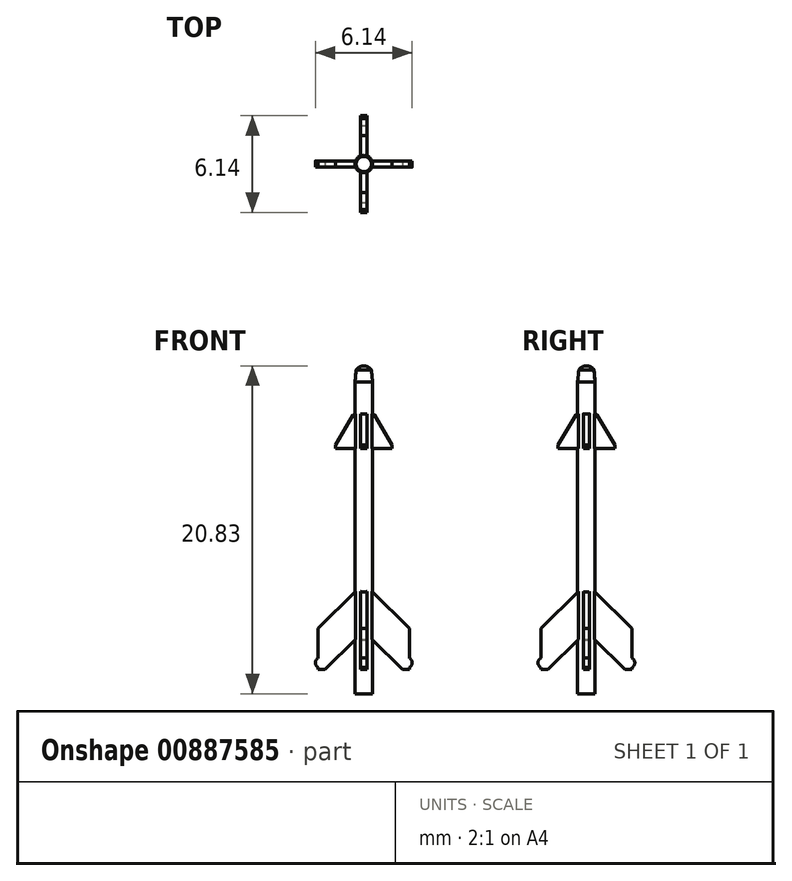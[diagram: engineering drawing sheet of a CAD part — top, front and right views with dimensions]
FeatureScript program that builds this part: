
annotation { "Feature Type Name" : "Feature", "Feature Type Description" : "" }
export const myFeature = defineFeature(function(context is Context, id is Id, definition is map)
    precondition{}
    {
        {
            var Q0;
            Q0=qCreatedBy(makeId("Front.planeOp"),FACE);
            var sketch = newSketch(context, id + "F0", { "sketchPlane" : qUnion([Q0])});
            skLineSegment(sketch, "E0", {"start": v(0, 0) * mm, "end": v(0, 20.83) * mm});
            skLineSegment(sketch, "E1", {"start": v(0.56, 19.8) * mm, "end": v(0.56, 0) * mm});
            skLineSegment(sketch, "E2", {"start": v(0.56, 0) * mm, "end": v(0, 0) * mm});
            skLineSegment(sketch, "E3", {"start": v(0, 20.83) * mm, "end": v(1.85, 20.83) * mm, "construction": true});
            skLineSegment(sketch, "E4", {"start": v(0.56, 19.8) * mm, "end": v(0.49, 20.56) * mm});
            skArc(sketch, "E5", {"start": v(0.49, 20.56) * mm, "mid": v(0.28, 20.76) * mm, "end": v(0, 20.83) * mm});
            skSolve(sketch);
        }
        {
            var Q0;
            Q0=qSketchRegion(id+"F0",true);
            var Q1;
            Q1=sQuery(id+"F0.wireOp",EDGE,"E0");
            revolve(context, id + "F1", {"surfaceOperationType" : NewSurfaceOperationType.NEW, "entities" : qUnion([Q0]), "axis" : qUnion([Q1]), "revolveType" : RevolveType.FULL});
        }
        {
            var Q0;
            Q0=qCreatedBy(makeId("Front.planeOp"),FACE);
            var sketch = newSketch(context, id + "F2", { "sketchPlane" : qUnion([Q0])});
            skLineSegment(sketch, "E6", {"start": v(0.38, 6.63) * mm, "end": v(-0.38, 6.63) * mm});
            skLineSegment(sketch, "E7", {"start": v(-2.9, 4.15) * mm, "end": v(-0.38, 6.63) * mm});
            skLineSegment(sketch, "E8", {"start": v(-2.9, 4.15) * mm, "end": v(-2.9, 2.27) * mm});
            skLineSegment(sketch, "E9", {"start": v(2.9, 2.27) * mm, "end": v(2.9, 4.15) * mm});
            skLineSegment(sketch, "E10", {"start": v(0.38, 6.63) * mm, "end": v(2.9, 4.15) * mm});
            skLineSegment(sketch, "E11", {"start": v(0, 0) * mm, "end": v(0, 6.63) * mm, "construction": true});
            skLineSegment(sketch, "E12", {"start": v(-0.56, -0.14) * mm, "end": v(-0.56, 4.02) * mm, "construction": true});
            skLineSegment(sketch, "E13.0", {"start": v(0.56, 19.8) * mm, "end": v(-0.56, 19.8) * mm});
            skPoint(sketch, "E14", {"position": v(-0.56, 6.46) * mm});
            skLineSegment(sketch, "E15", {"start": v(-2.9, 1.53) * mm, "end": v(-2.9, 1.67) * mm});
            skArc(sketch, "E16", {"start": v(-2.9, 2.27) * mm, "mid": v(-3.07, 1.97) * mm, "end": v(-2.9, 1.67) * mm});
            skArc(sketch, "E17", {"start": v(2.9, 1.67) * mm, "mid": v(3.07, 1.97) * mm, "end": v(2.9, 2.27) * mm});
            skLineSegment(sketch, "E18", {"start": v(-1.8, 15.6) * mm, "end": v(1.8, 15.6) * mm});
            skLineSegment(sketch, "E19", {"start": v(0, 15.6) * mm, "end": v(0, 0) * mm, "construction": true});
            skLineSegment(sketch, "E20", {"start": v(-0.56, 19.8) * mm, "end": v(-0.56, 14.02) * mm, "construction": true});
            skLineSegment(sketch, "E21", {"start": v(-1.8, 15.6) * mm, "end": v(-1.8, 15.8) * mm});
            skLineSegment(sketch, "E22", {"start": v(-1.8, 15.8) * mm, "end": v(-0.68, 17.7) * mm});
            skLineSegment(sketch, "E23", {"start": v(1.8, 15.6) * mm, "end": v(1.8, 15.8) * mm});
            skLineSegment(sketch, "E24", {"start": v(1.8, 15.8) * mm, "end": v(0.68, 17.7) * mm});
            skArc(sketch, "E25", {"start": v(-0.56, 17.78) * mm, "mid": v(-0.63, 17.76) * mm, "end": v(-0.68, 17.7) * mm});
            skArc(sketch, "E26", {"start": v(0.68, 17.7) * mm, "mid": v(0.63, 17.76) * mm, "end": v(0.56, 17.78) * mm});
            skLineSegment(sketch, "E27", {"start": v(-0.56, 17.78) * mm, "end": v(0.56, 17.78) * mm});
            skLineSegment(sketch, "E28", {"start": v(-2.45, 1.53) * mm, "end": v(-0.26, 3.7) * mm});
            skLineSegment(sketch, "E29", {"start": v(-0.26, 3.7) * mm, "end": v(0.26, 3.7) * mm});
            skLineSegment(sketch, "E30", {"start": v(0.26, 3.7) * mm, "end": v(2.45, 1.53) * mm});
            skLineSegment(sketch, "E31", {"start": v(2.9, 1.67) * mm, "end": v(2.9, 1.53) * mm});
            skLineSegment(sketch, "E32", {"start": v(-2.45, 1.53) * mm, "end": v(-2.9, 1.53) * mm});
            skLineSegment(sketch, "E33", {"start": v(2.45, 1.53) * mm, "end": v(2.9, 1.53) * mm});
            skPoint(sketch, "E34", {"position": v(-0.56, 3.4) * mm});
            skSolve(sketch);
        }
        {
            var Q0;
            Q0=qSketchRegion(id+"F2",true);
            extrude(context, id + "F3", {"entities" : qUnion([Q0]), "operationType" : NewBodyOperationType.ADD, "depth" : .4 * mm, "offsetDistance" : 25 * mm, "symmetric" : true});
        }
        {
            var Q0;
            Q0=makeQuery(id+"F1.opRevolve","SWEPT_BODY",BODY,{"disambiguationData":[OSD([sQuery(id+"F0.wireOp",EDGE,"E0"),sQuery(id+"F0.wireOp",EDGE,"E1"),sQuery(id+"F0.wireOp",EDGE,"E2"),sQuery(id+"F0.wireOp",EDGE,"m1K1lCZm-MTc8-Btmt-IA6e-LtdyprMEJuD3")])]});
            var Q1;
            Q1=makeQuery(id+"F1.opRevolve","SWEPT_FACE",FACE,{"disambiguationData":[OSD([sQuery(id+"F0.wireOp",EDGE,"E1")])]});
            circularPattern(context, id + "F4", {"entities" : qUnion([Q0]), "axis" : qUnion([Q1]), "angle" : 360 * degree, "instanceCount" : 4, "equalSpace" : true, "computeTransformsWithoutBuiltin" : true});
        }
    });
